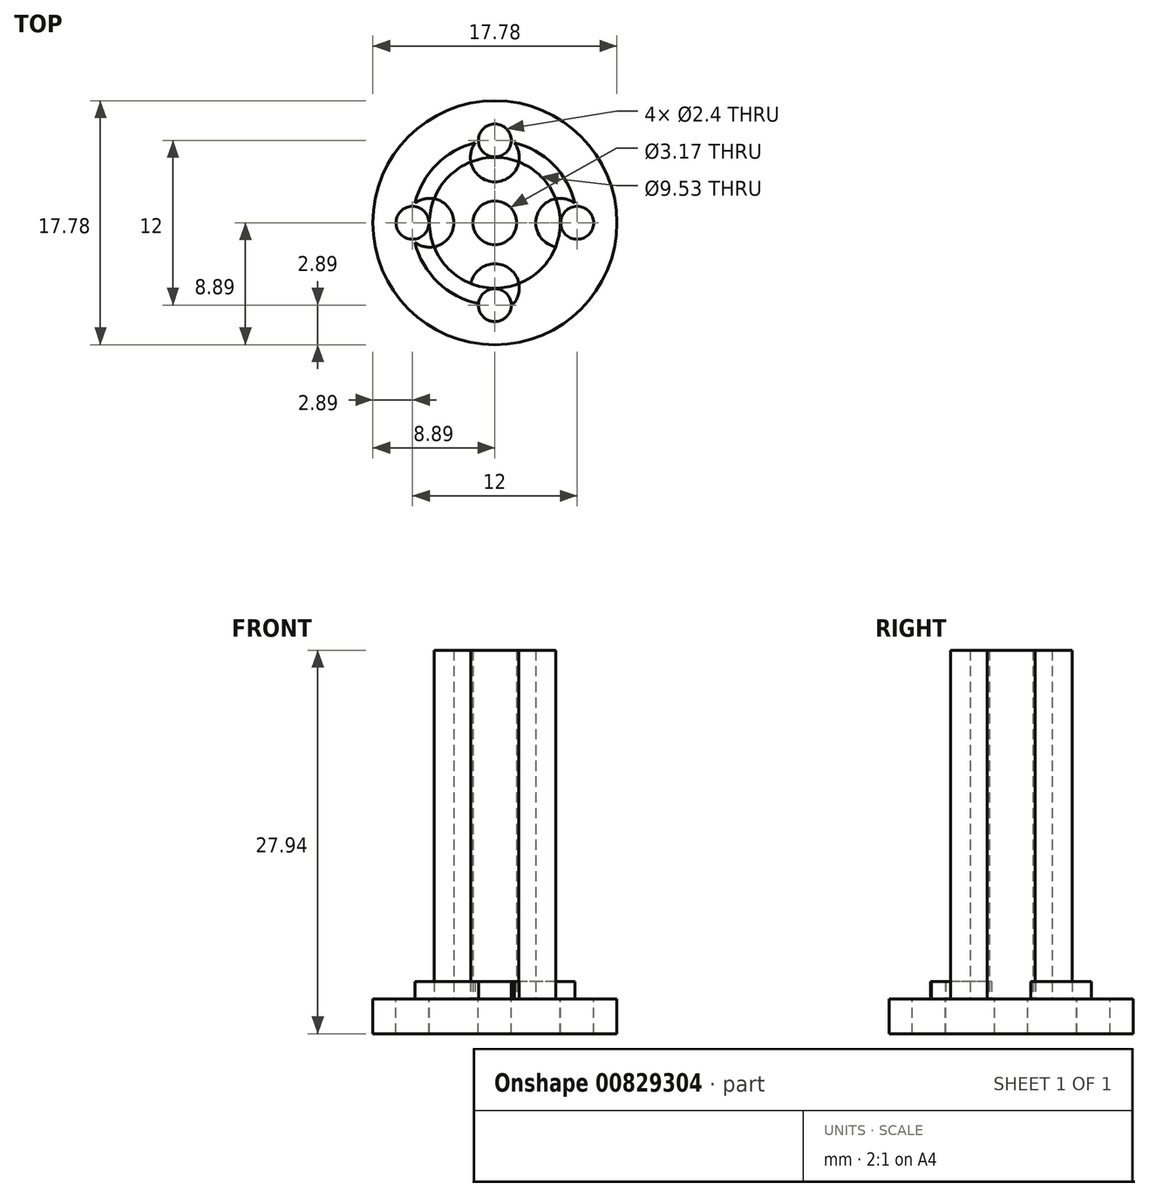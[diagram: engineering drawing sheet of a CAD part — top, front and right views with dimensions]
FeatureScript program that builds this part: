
annotation { "Feature Type Name" : "Feature", "Feature Type Description" : "" }
export const myFeature = defineFeature(function(context is Context, id is Id, definition is map)
    precondition{}
    {
        {
            var Q0;
            Q0=qCreatedBy(makeId("Top.planeOp"),FACE);
            var sketch = newSketch(context, id + "F0", { "sketchPlane" : qUnion([Q0])});
            skCircle(sketch, "E0", {"center": v(0, 0) * mm, "radius": 8.9 * mm});
            skCircle(sketch, "E1", {"center": v(0, 0) * mm, "radius": 1.59 * mm});
            skCircle(sketch, "E2", {"center": v(0, 0) * mm, "radius": 4.76 * mm});
            skArc(sketch, "E3", {"start": v(1.2, -5.88) * mm, "mid": v(4.24, -4.24) * mm, "end": v(5.88, -1.2) * mm});
            skCircle(sketch, "E4", {"center": v(6, 0) * mm, "radius": 1.2 * mm});
            skCircle(sketch, "E5", {"center": v(0, 6) * mm, "radius": 1.2 * mm});
            skCircle(sketch, "E6", {"center": v(-6, 0) * mm, "radius": 1.2 * mm});
            skCircle(sketch, "E7", {"center": v(0, -6) * mm, "radius": 1.2 * mm});
            skArc(sketch, "E8", {"start": v(-1.42, 5.83) * mm, "mid": v(0, 2.98) * mm, "end": v(1.42, 5.83) * mm});
            skArc(sketch, "E9", {"start": v(5.83, 1.42) * mm, "mid": v(2.98, 0) * mm, "end": v(5.83, -1.42) * mm});
            skArc(sketch, "E10", {"start": v(1.42, -5.83) * mm, "mid": v(0, -2.98) * mm, "end": v(-1.42, -5.83) * mm});
            skArc(sketch, "E11", {"start": v(-5.83, -1.42) * mm, "mid": v(-2.98, 0) * mm, "end": v(-5.83, 1.42) * mm});
            skArc(sketch, "E12.trimOffspring", {"start": v(5.88, 1.2) * mm, "mid": v(4.24, 4.24) * mm, "end": v(1.2, 5.88) * mm});
            skArc(sketch, "E13.trimOffspring", {"start": v(-1.2, 5.88) * mm, "mid": v(-4.24, 4.24) * mm, "end": v(-5.88, 1.2) * mm});
            skArc(sketch, "E14.trimOffspring", {"start": v(-5.88, -1.2) * mm, "mid": v(-4.24, -4.24) * mm, "end": v(-1.2, -5.88) * mm});
            skSolve(sketch);
        }
        {
            var Q0;
            {var subQ0=sQuery(id+"F0.wireOp",EDGE,"E8");var subQ1=sQuery(id+"F0.wireOp",EDGE,"E2");var subQ2=makeQuery(id+"F0.imprint","INTERSECT",VERTEX,{"disambiguationData":[OD(1.0)],"derivedFrom":[subQ1,subQ0]});Q0=makeQuery(id+"F0.imprint","IMPRINT",FACE,{"disambiguationData":[TD([[makeQuery(id+"F0.imprint","IMPRINT",EDGE,{"disambiguationData":[TD([[subQ2,-1.0]])],"derivedFrom":subQ1}),-1.0]])]});}
            var Q1;
            {var subQ3=sQuery(id+"F0.wireOp",EDGE,"E8");var subQ5=sQuery(id+"F0.wireOp",EDGE,"E2");var subQ6=makeQuery(id+"F0.imprint","INTERSECT",VERTEX,{"disambiguationData":[OD(0.0)],"derivedFrom":[subQ5,subQ3]});Q1=makeQuery(id+"F0.imprint","IMPRINT",FACE,{"disambiguationData":[TD([[makeQuery(id+"F0.imprint","IMPRINT",EDGE,{"disambiguationData":[TD([[subQ6,-1.0]])],"derivedFrom":subQ5}),-1.0]])]});}
            var Q2;
            {var subQ0=sQuery(id+"F0.wireOp",EDGE,"E8");var subQ1=sQuery(id+"F0.wireOp",EDGE,"E2");var subQ2=makeQuery(id+"F0.imprint","INTERSECT",VERTEX,{"disambiguationData":[OD(0.0)],"derivedFrom":[subQ1,subQ0]});Q2=makeQuery(id+"F0.imprint","IMPRINT",FACE,{"disambiguationData":[TD([[makeQuery(id+"F0.imprint","IMPRINT",EDGE,{"disambiguationData":[TD([[subQ2,1.0]])],"derivedFrom":subQ1}),-1.0]])]});}
            var Q3;
            {var subQ4=sQuery(id+"F0.wireOp",EDGE,"E9");var subQ5=sQuery(id+"F0.wireOp",EDGE,"E2");var subQ6=makeQuery(id+"F0.imprint","INTERSECT",VERTEX,{"disambiguationData":[OD(0.0)],"derivedFrom":[subQ5,subQ4]});Q3=makeQuery(id+"F0.imprint","IMPRINT",FACE,{"disambiguationData":[TD([[makeQuery(id+"F0.imprint","IMPRINT",EDGE,{"disambiguationData":[TD([[subQ6,1.0]])],"derivedFrom":subQ5}),-1.0]])]});}
            var Q4;
            {var subQ0=sQuery(id+"F0.wireOp",EDGE,"E10");var subQ1=sQuery(id+"F0.wireOp",EDGE,"E2");var subQ2=makeQuery(id+"F0.imprint","INTERSECT",VERTEX,{"disambiguationData":[OD(1.0)],"derivedFrom":[subQ1,subQ0]});Q4=makeQuery(id+"F0.imprint","IMPRINT",FACE,{"disambiguationData":[TD([[makeQuery(id+"F0.imprint","IMPRINT",EDGE,{"disambiguationData":[TD([[subQ2,-1.0]])],"derivedFrom":subQ1}),-1.0]])]});}
            var Q5;
            {var subQ4=sQuery(id+"F0.wireOp",EDGE,"E10");var subQ7=sQuery(id+"F0.wireOp",EDGE,"E2");var subQ8=makeQuery(id+"F0.imprint","INTERSECT",VERTEX,{"disambiguationData":[OD(0.0)],"derivedFrom":[subQ7,subQ4]});Q5=makeQuery(id+"F0.imprint","IMPRINT",FACE,{"disambiguationData":[TD([[makeQuery(id+"F0.imprint","IMPRINT",EDGE,{"disambiguationData":[TD([[subQ8,-1.0]])],"derivedFrom":subQ7}),-1.0]])]});}
            var Q6;
            {var subQ0=sQuery(id+"F0.wireOp",EDGE,"E11");var subQ1=sQuery(id+"F0.wireOp",EDGE,"E2");var subQ2=makeQuery(id+"F0.imprint","INTERSECT",VERTEX,{"disambiguationData":[OD(1.0)],"derivedFrom":[subQ1,subQ0]});Q6=makeQuery(id+"F0.imprint","IMPRINT",FACE,{"disambiguationData":[TD([[makeQuery(id+"F0.imprint","IMPRINT",EDGE,{"disambiguationData":[TD([[subQ2,-1.0]])],"derivedFrom":subQ1}),-1.0]])]});}
            var Q7;
            {var subQ0=sQuery(id+"F0.wireOp",EDGE,"E11");var subQ1=sQuery(id+"F0.wireOp",EDGE,"E3");var subQ2=makeQuery(id+"F0.imprint","INTERSECT",VERTEX,{"disambiguationData":[OD(0.0)],"derivedFrom":[subQ1,subQ0]});Q7=makeQuery(id+"F0.imprint","IMPRINT",FACE,{"disambiguationData":[TD([[makeQuery(id+"F0.imprint","IMPRINT",EDGE,{"disambiguationData":[TD([[subQ2,-1.0]])],"derivedFrom":subQ1}),-1.0]])]});}
            var Q8;
            {var subQ0=sQuery(id+"F0.wireOp",EDGE,"E6");var subQ1=sQuery(id+"F0.wireOp",EDGE,"E3");var subQ2=makeQuery(id+"F0.imprint","INTERSECT",VERTEX,{"disambiguationData":[OD(1.0)],"derivedFrom":[subQ1,subQ0]});Q8=makeQuery(id+"F0.imprint","IMPRINT",FACE,{"disambiguationData":[TD([[makeQuery(id+"F0.imprint","IMPRINT",EDGE,{"disambiguationData":[TD([[subQ2,-1.0]])],"derivedFrom":subQ1}),-1.0]])]});}
            var Q9;
            {var subQ4=sQuery(id+"F0.wireOp",EDGE,"E11");var subQ7=sQuery(id+"F0.wireOp",EDGE,"E2");var subQ8=makeQuery(id+"F0.imprint","INTERSECT",VERTEX,{"disambiguationData":[OD(0.0)],"derivedFrom":[subQ7,subQ4]});Q9=makeQuery(id+"F0.imprint","IMPRINT",FACE,{"disambiguationData":[TD([[makeQuery(id+"F0.imprint","IMPRINT",EDGE,{"disambiguationData":[TD([[subQ8,-1.0]])],"derivedFrom":subQ7}),-1.0]])]});}
            var Q10;
            {var subQ0=sQuery(id+"F0.wireOp",EDGE,"E5");var subQ1=sQuery(id+"F0.wireOp",EDGE,"E3");var subQ2=makeQuery(id+"F0.imprint","INTERSECT",VERTEX,{"disambiguationData":[OD(1.0)],"derivedFrom":[subQ1,subQ0]});Q10=makeQuery(id+"F0.imprint","IMPRINT",FACE,{"disambiguationData":[TD([[makeQuery(id+"F0.imprint","IMPRINT",EDGE,{"disambiguationData":[TD([[subQ2,-1.0]])],"derivedFrom":subQ1}),-1.0]])]});}
            var Q11;
            {var subQ0=sQuery(id+"F0.wireOp",EDGE,"E8");var subQ1=sQuery(id+"F0.wireOp",EDGE,"E3");var subQ2=makeQuery(id+"F0.imprint","INTERSECT",VERTEX,{"disambiguationData":[OD(0.0)],"derivedFrom":[subQ1,subQ0]});Q11=makeQuery(id+"F0.imprint","IMPRINT",FACE,{"disambiguationData":[TD([[makeQuery(id+"F0.imprint","IMPRINT",EDGE,{"disambiguationData":[TD([[subQ2,-1.0]])],"derivedFrom":subQ1}),-1.0]])]});}
            var Q12;
            {var subQ0=sQuery(id+"F0.wireOp",EDGE,"E9");var subQ1=sQuery(id+"F0.wireOp",EDGE,"E3");var subQ2=makeQuery(id+"F0.imprint","INTERSECT",VERTEX,{"disambiguationData":[OD(0.0)],"derivedFrom":[subQ1,subQ0]});Q12=makeQuery(id+"F0.imprint","IMPRINT",FACE,{"disambiguationData":[TD([[makeQuery(id+"F0.imprint","IMPRINT",EDGE,{"disambiguationData":[TD([[subQ2,1.0]])],"derivedFrom":subQ1}),-1.0]])]});}
            var Q13;
            Q13=makeQuery(id+"F0.imprint","IMPRINT",FACE,{"disambiguationData":[TD([[makeQuery(id+"F0.imprint","IMPRINT",EDGE,{"derivedFrom":sQuery(id+"F0.wireOp",EDGE,"E0")}),1.0]])]});
            var Q14;
            {var subQ0=sQuery(id+"F0.wireOp",EDGE,"E9");var subQ1=sQuery(id+"F0.wireOp",EDGE,"E3");var subQ2=makeQuery(id+"F0.imprint","INTERSECT",VERTEX,{"disambiguationData":[OD(1.0)],"derivedFrom":[subQ1,subQ0]});Q14=makeQuery(id+"F0.imprint","IMPRINT",FACE,{"disambiguationData":[TD([[makeQuery(id+"F0.imprint","IMPRINT",EDGE,{"disambiguationData":[TD([[subQ2,-1.0]])],"derivedFrom":subQ1}),-1.0]])]});}
            var Q15;
            {var subQ0=sQuery(id+"F0.wireOp",EDGE,"E7");var subQ1=sQuery(id+"F0.wireOp",EDGE,"E3");var subQ2=makeQuery(id+"F0.imprint","INTERSECT",VERTEX,{"disambiguationData":[OD(1.0)],"derivedFrom":[subQ1,subQ0]});Q15=makeQuery(id+"F0.imprint","IMPRINT",FACE,{"disambiguationData":[TD([[makeQuery(id+"F0.imprint","IMPRINT",EDGE,{"disambiguationData":[TD([[subQ2,-1.0]])],"derivedFrom":subQ1}),-1.0]])]});}
            var Q16;
            {var subQ0=sQuery(id+"F0.wireOp",EDGE,"E10");var subQ1=sQuery(id+"F0.wireOp",EDGE,"E3");var subQ2=makeQuery(id+"F0.imprint","INTERSECT",VERTEX,{"disambiguationData":[OD(0.0)],"derivedFrom":[subQ1,subQ0]});Q16=makeQuery(id+"F0.imprint","IMPRINT",FACE,{"disambiguationData":[TD([[makeQuery(id+"F0.imprint","IMPRINT",EDGE,{"disambiguationData":[TD([[subQ2,-1.0]])],"derivedFrom":subQ1}),-1.0]])]});}
            extrude(context, id + "F1", {"entities" : qUnion([Q0, Q1, Q2, Q3, Q4, Q5, Q6, Q7, Q8, Q9, Q10, Q11, Q12, Q13, Q14, Q15, Q16]), "depth" : -2.54 * mm, "offsetDistance" : 25.4 * mm});
        }
        {
            var Q0;
            Q0=makeQuery(id+"F0.imprint","IMPRINT",FACE,{"disambiguationData":[TD([[makeQuery(id+"F0.imprint","IMPRINT",EDGE,{"derivedFrom":sQuery(id+"F0.wireOp",EDGE,"E1")}),-1.0]])]});
            extrude(context, id + "F2", {"entities" : qUnion([Q0]), "depth" : 25.4 * mm, "offsetDistance" : 25.4 * mm});
        }
        {
            var Q0;
            {var subQ0=sQuery(id+"F0.wireOp",EDGE,"E11");var subQ1=sQuery(id+"F0.wireOp",EDGE,"E2");var subQ2=makeQuery(id+"F0.imprint","INTERSECT",VERTEX,{"disambiguationData":[OD(1.0)],"derivedFrom":[subQ1,subQ0]});Q0=makeQuery(id+"F0.imprint","IMPRINT",FACE,{"disambiguationData":[TD([[makeQuery(id+"F0.imprint","IMPRINT",EDGE,{"disambiguationData":[TD([[subQ2,-1.0]])],"derivedFrom":subQ1}),-1.0]])]});}
            var Q1;
            {var subQ0=sQuery(id+"F0.wireOp",EDGE,"E10");var subQ1=sQuery(id+"F0.wireOp",EDGE,"E2");var subQ2=makeQuery(id+"F0.imprint","INTERSECT",VERTEX,{"disambiguationData":[OD(1.0)],"derivedFrom":[subQ1,subQ0]});Q1=makeQuery(id+"F0.imprint","IMPRINT",FACE,{"disambiguationData":[TD([[makeQuery(id+"F0.imprint","IMPRINT",EDGE,{"disambiguationData":[TD([[subQ2,-1.0]])],"derivedFrom":subQ1}),-1.0]])]});}
            var Q2;
            {var subQ0=sQuery(id+"F0.wireOp",EDGE,"E8");var subQ1=sQuery(id+"F0.wireOp",EDGE,"E2");var subQ2=makeQuery(id+"F0.imprint","INTERSECT",VERTEX,{"disambiguationData":[OD(0.0)],"derivedFrom":[subQ1,subQ0]});Q2=makeQuery(id+"F0.imprint","IMPRINT",FACE,{"disambiguationData":[TD([[makeQuery(id+"F0.imprint","IMPRINT",EDGE,{"disambiguationData":[TD([[subQ2,1.0]])],"derivedFrom":subQ1}),-1.0]])]});}
            var Q3;
            {var subQ0=sQuery(id+"F0.wireOp",EDGE,"E8");var subQ1=sQuery(id+"F0.wireOp",EDGE,"E2");var subQ2=makeQuery(id+"F0.imprint","INTERSECT",VERTEX,{"disambiguationData":[OD(1.0)],"derivedFrom":[subQ1,subQ0]});Q3=makeQuery(id+"F0.imprint","IMPRINT",FACE,{"disambiguationData":[TD([[makeQuery(id+"F0.imprint","IMPRINT",EDGE,{"disambiguationData":[TD([[subQ2,-1.0]])],"derivedFrom":subQ1}),-1.0]])]});}
            extrude(context, id + "F3", {"entities" : qUnion([Q0, Q1, Q2, Q3]), "depth" : 1.27 * mm, "offsetDistance" : 25.4 * mm});
        }
    });
